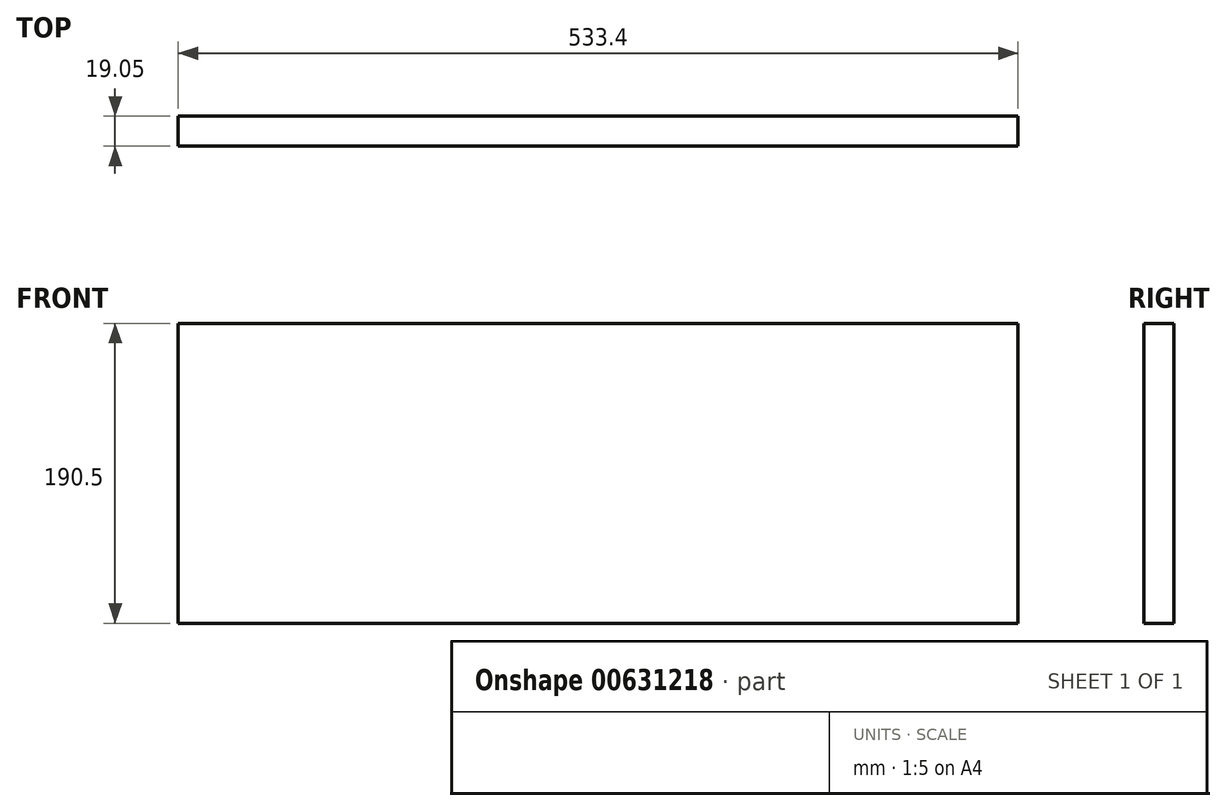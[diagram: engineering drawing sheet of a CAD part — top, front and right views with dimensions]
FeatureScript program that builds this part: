
annotation { "Feature Type Name" : "Feature", "Feature Type Description" : "" }
export const myFeature = defineFeature(function(context is Context, id is Id, definition is map)
    precondition{}
    {
        {
            var Q0;
            Q0=qCreatedBy(makeId("Front.planeOp"),FACE);
            var sketch = newSketch(context, id + "F0", { "sketchPlane" : qUnion([Q0])});
            skLineSegment(sketch, "E0.bottom", {"start": v(0, 0) * mm, "end": v(533.4, 0) * mm});
            skLineSegment(sketch, "E0.top", {"start": v(0, 190.5) * mm, "end": v(533.4, 190.5) * mm});
            skLineSegment(sketch, "E0.left", {"start": v(0, 0) * mm, "end": v(0, 190.5) * mm});
            skLineSegment(sketch, "E0.right", {"start": v(533.4, 0) * mm, "end": v(533.4, 190.5) * mm});
            skSolve(sketch);
        }
        {
            var Q0;
            Q0=qSketchRegion(id+"Fzz42SO8jX8z24B_0",true);
            var Q1;
            Q1=makeQuery(id+"F0.imprint","IMPRINT",FACE,{"disambiguationData":[TD([[makeQuery(id+"F0.imprint","IMPRINT",EDGE,{"derivedFrom":sQuery(id+"F0.wireOp",EDGE,"E0.bottom")}),1.0]])]});
            extrude(context, id + "F1", {"entities" : qUnion([Q0, Q1]), "depth" : -19.05 * mm, "offsetDistance" : 25.4 * mm});
        }
    });
